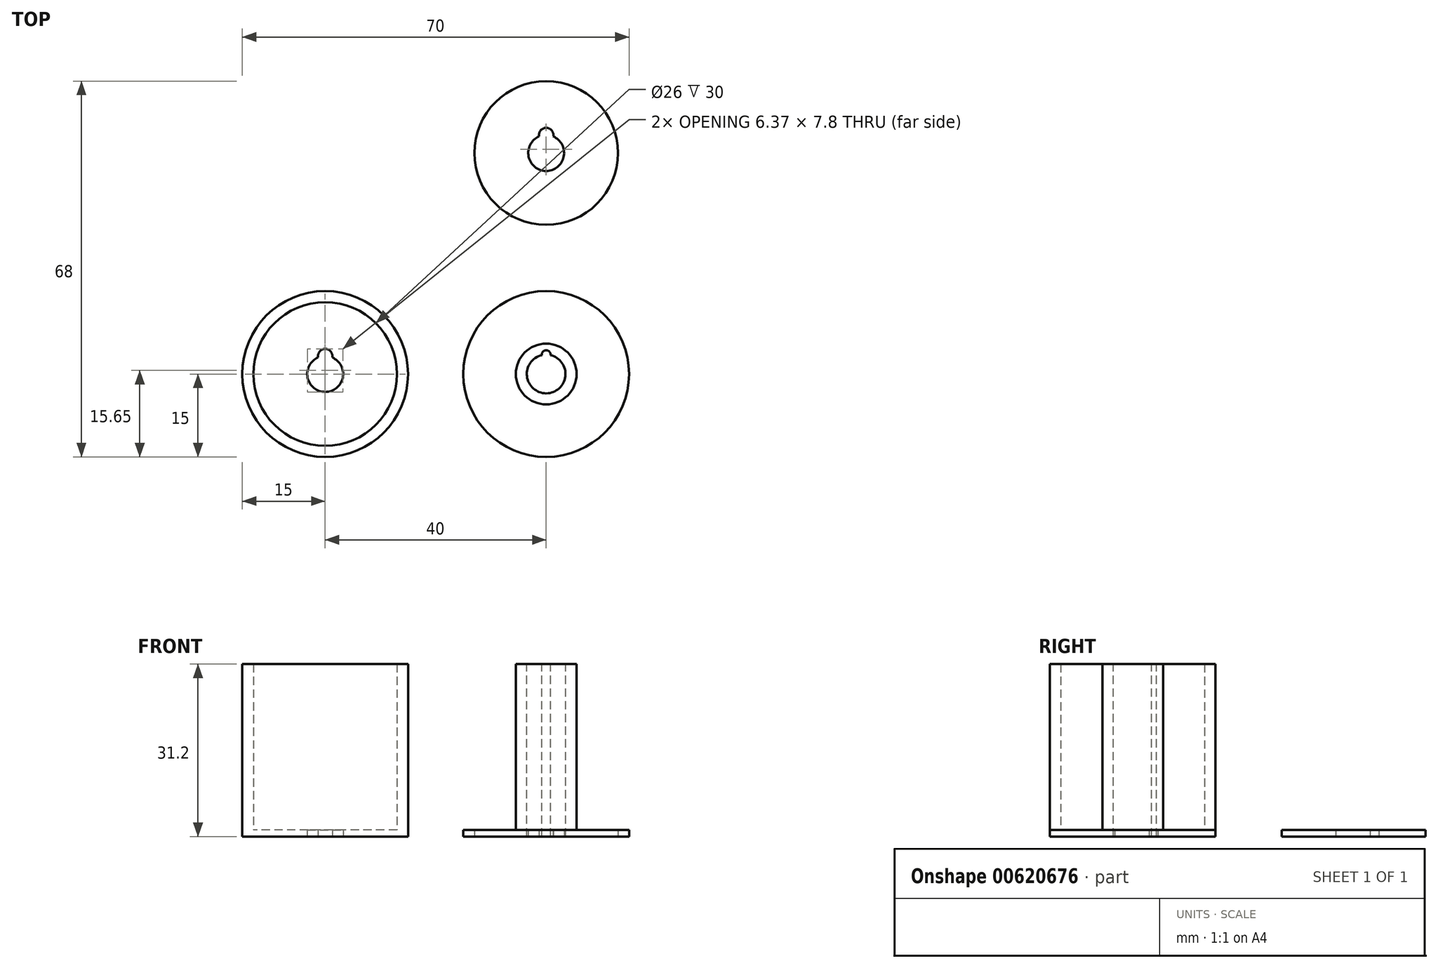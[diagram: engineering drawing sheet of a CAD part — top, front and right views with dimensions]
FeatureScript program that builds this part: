
annotation { "Feature Type Name" : "Feature", "Feature Type Description" : "" }
export const myFeature = defineFeature(function(context is Context, id is Id, definition is map)
    precondition{}
    {
        {
            var Q0;
            Q0=qCreatedBy(makeId("Top.planeOp"),FACE);
            var sketch = newSketch(context, id + "F0", { "sketchPlane" : qUnion([Q0])});
            skCircle(sketch, "E0", {"center": v(0, 0) * mm, "radius": 15 * mm});
            skCircle(sketch, "E1", {"center": v(0, 40) * mm, "radius": 13 * mm});
            skArc(sketch, "E2", {"start": v(-1.27, 43) * mm, "mid": v(0, 36.75) * mm, "end": v(1.27, 43) * mm});
            skArc(sketch, "E3", {"start": v(1.27, 43) * mm, "mid": v(0, 44.55) * mm, "end": v(-1.27, 43) * mm});
            skCircle(sketch, "E4", {"center": v(-40, 0) * mm, "radius": 15 * mm});
            skArc(sketch, "E5", {"start": v(-41.27, 3) * mm, "mid": v(-40, -3.25) * mm, "end": v(-38.73, 3) * mm});
            skArc(sketch, "E6", {"start": v(-38.73, 3) * mm, "mid": v(-40, 4.55) * mm, "end": v(-41.27, 2.99) * mm});
            skSolve(sketch);
        }
        {
            var Q0;
            Q0 = qSketchRegion(id + "F0", true);
            extrude(context, id + "F1", {"entities" : qUnion([Q0]), "depth" : 1.2 * mm, "offsetDistance" : 25 * mm});
        }
        {
            var Q0;
            Q0=makeQuery(id+"F1.opExtrude","CAP_FACE",FACE,{"disambiguationData":[OSD([sQuery(id+"F0.wireOp",EDGE,"E0")])],"isStart":false});
            var sketch = newSketch(context, id + "F2", { "sketchPlane" : qUnion([Q0])});
            skArc(sketch, "E7", {"start": v(-0.8, 3.4) * mm, "mid": v(0, -3.5) * mm, "end": v(0.8, 3.4) * mm});
            skCircle(sketch, "E8", {"center": v(0, 0) * mm, "radius": 5.5 * mm});
            skArc(sketch, "E9", {"start": v(0.8, 3.4) * mm, "mid": v(0, 4.3) * mm, "end": v(-0.8, 3.4) * mm});
            skCircle(sketch, "E10", {"center": v(-40, 0) * mm, "radius": 15 * mm});
            skCircle(sketch, "E11", {"center": v(-40, 0) * mm, "radius": 13 * mm});
            skSolve(sketch);
        }
        {
            var Q0;
            Q0=makeQuery(id+"F2.imprint","IMPRINT",FACE,{"disambiguationData":[TD([[makeQuery(id+"F2.imprint","IMPRINT",EDGE,{"derivedFrom":sQuery(id+"F2.wireOp",EDGE,"E7")}),1.0]])]});
            extrude(context, id + "F3", {"entities" : qUnion([Q0]), "operationType" : NewBodyOperationType.REMOVE, "endBound" : BoundingType.UP_TO_NEXT, "oppositeDirection" : true, "depth" : 25 * mm, "offsetDistance" : 25 * mm});
        }
        {
            var Q0;
            Q0 = qSketchRegion(id + "F2", true);
            extrude(context, id + "F4", {"entities" : qUnion([Q0]), "operationType" : NewBodyOperationType.ADD, "depth" : 30 * mm, "offsetDistance" : 25 * mm});
        }
    });
